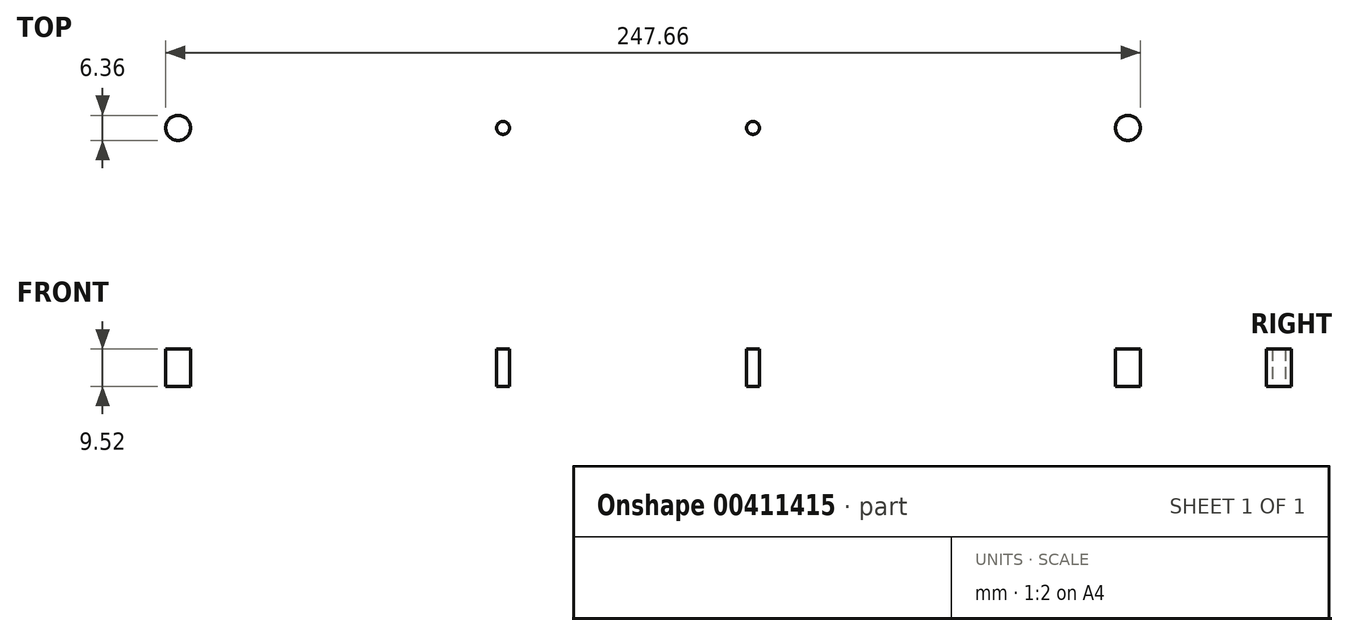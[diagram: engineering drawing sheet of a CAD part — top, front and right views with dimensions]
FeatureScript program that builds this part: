
annotation { "Feature Type Name" : "Feature", "Feature Type Description" : "" }
export const myFeature = defineFeature(function(context is Context, id is Id, definition is map)
    precondition{}
    {
        {
            var Q0;
            Q0=qCreatedBy(makeId("Top.planeOp"),FACE);
            var sketch = newSketch(context, id + "F0", { "sketchPlane" : qUnion([Q0])});
            skLineSegment(sketch, "E0", {"start": v(-152.4, -38.1) * mm, "end": v(-152.4, 38.1) * mm});
            skLineSegment(sketch, "E1", {"start": v(-152.4, 38.1) * mm, "end": v(127, 38.1) * mm});
            skLineSegment(sketch, "E2", {"start": v(127, 38.1) * mm, "end": v(127, -38.1) * mm});
            skLineSegment(sketch, "E3", {"start": v(127, -38.1) * mm, "end": v(-152.4, -38.1) * mm});
            skSolve(sketch);
        }
        {
            var Q0;
            Q0=makeQuery(id+"F0.imprint","IMPRINT",FACE,{"disambiguationData":[TD([[makeQuery(id+"F0.imprint","IMPRINT",EDGE,{"derivedFrom":sQuery(id+"F0.wireOp",EDGE,"E0")}),-1.0]])]});
            extrude(context, id + "F1", {"entities" : qUnion([Q0]), "endBound" : BoundingType.SYMMETRIC, "depth" : 9.52 * mm});
        }
        {
            var Q0;
            Q0=makeQuery(id+"F1.opExtrude","CAP_FACE",FACE,{"disambiguationData":[OSD([sQuery(id+"F0.wireOp",EDGE,"E0"),sQuery(id+"F0.wireOp",EDGE,"E1"),sQuery(id+"F0.wireOp",EDGE,"E2"),sQuery(id+"F0.wireOp",EDGE,"E3")])],"isStart":true});
            var sketch = newSketch(context, id + "F2", { "sketchPlane" : qUnion([Q0])});
            skLineSegment(sketch, "E4", {"start": v(-152.4, 0) * mm, "end": v(127, 0) * mm, "construction": true});
            skLineSegment(sketch, "E5", {"start": v(-152.4, 12.7) * mm, "end": v(127, 12.7) * mm, "construction": true});
            skCircle(sketch, "E6", {"center": v(-139.7, 12.7) * mm, "radius": 3.18 * mm});
            skCircle(sketch, "E7", {"center": v(-57.15, 12.7) * mm, "radius": 1.65 * mm});
            skLineSegment(sketch, "E8", {"start": v(0, 38.1) * mm, "end": v(0, -38.1) * mm, "construction": true});
            skCircle(sketch, "E9", {"center": v(6.35, 12.7) * mm, "radius": 1.65 * mm});
            skCircle(sketch, "E10", {"center": v(101.6, 12.7) * mm, "radius": 3.18 * mm});
            skCircle(sketch, "E11.MirrorC", {"center": v(101.6, -12.7) * mm, "radius": 3.18 * mm});
            skCircle(sketch, "E12.MirrorC", {"center": v(6.35, -12.7) * mm, "radius": 1.65 * mm});
            skCircle(sketch, "E13.MirrorC", {"center": v(-57.15, -12.7) * mm, "radius": 1.65 * mm});
            skCircle(sketch, "E14.MirrorC", {"center": v(-139.7, -12.7) * mm, "radius": 3.18 * mm});
            skSolve(sketch);
        }
        {
            var Q0;
            Q0=makeQuery(id+"F2.imprint","IMPRINT",FACE,{"disambiguationData":[TD([[makeQuery(id+"F2.imprint","IMPRINT",EDGE,{"derivedFrom":sQuery(id+"F2.wireOp",EDGE,"E6")}),1.0]])]});
            var Q1;
            Q1=makeQuery(id+"F2.imprint","IMPRINT",FACE,{"disambiguationData":[TD([[makeQuery(id+"F2.imprint","IMPRINT",EDGE,{"derivedFrom":sQuery(id+"F2.wireOp",EDGE,"E14.MirrorC")}),-1.0]])]});
            var Q2;
            Q2=makeQuery(id+"F2.imprint","IMPRINT",FACE,{"disambiguationData":[TD([[makeQuery(id+"F2.imprint","IMPRINT",EDGE,{"derivedFrom":sQuery(id+"F2.wireOp",EDGE,"E13.MirrorC")}),-1.0]])]});
            var Q3;
            Q3=makeQuery(id+"F2.imprint","IMPRINT",FACE,{"disambiguationData":[TD([[makeQuery(id+"F2.imprint","IMPRINT",EDGE,{"derivedFrom":sQuery(id+"F2.wireOp",EDGE,"E7")}),1.0]])]});
            var Q4;
            Q4=makeQuery(id+"F2.imprint","IMPRINT",FACE,{"disambiguationData":[TD([[makeQuery(id+"F2.imprint","IMPRINT",EDGE,{"derivedFrom":sQuery(id+"F2.wireOp",EDGE,"E9")}),1.0]])]});
            var Q5;
            Q5=makeQuery(id+"F2.imprint","IMPRINT",FACE,{"disambiguationData":[TD([[makeQuery(id+"F2.imprint","IMPRINT",EDGE,{"derivedFrom":sQuery(id+"F2.wireOp",EDGE,"E12.MirrorC")}),-1.0]])]});
            var Q6;
            Q6=makeQuery(id+"F2.imprint","IMPRINT",FACE,{"disambiguationData":[TD([[makeQuery(id+"F2.imprint","IMPRINT",EDGE,{"derivedFrom":sQuery(id+"F2.wireOp",EDGE,"E11.MirrorC")}),-1.0]])]});
            var Q7;
            Q7=makeQuery(id+"F2.imprint","IMPRINT",FACE,{"disambiguationData":[TD([[makeQuery(id+"F2.imprint","IMPRINT",EDGE,{"derivedFrom":sQuery(id+"F2.wireOp",EDGE,"E10")}),1.0]])]});
            extrude(context, id + "F3", {"entities" : qUnion([Q0, Q1, Q2, Q3, Q4, Q5, Q6, Q7]), "operationType" : NewBodyOperationType.REMOVE, "endBound" : BoundingType.THROUGH_ALL, "oppositeDirection" : true, "depth" : 25.4 * mm});
        }
    });
